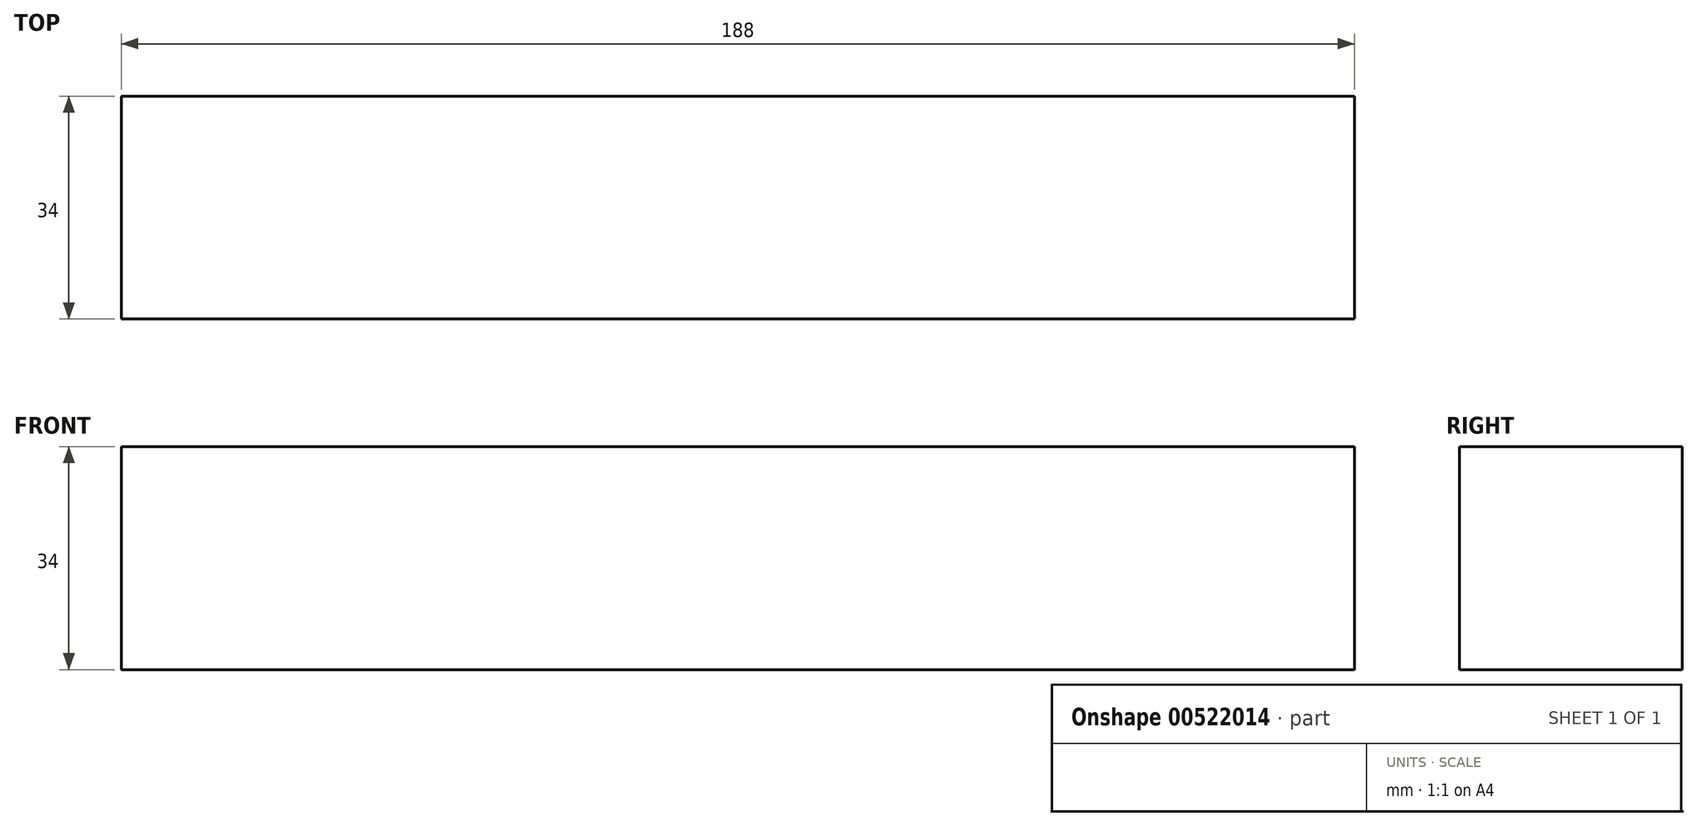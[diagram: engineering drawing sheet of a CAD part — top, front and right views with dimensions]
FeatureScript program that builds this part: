
annotation { "Feature Type Name" : "Feature", "Feature Type Description" : "" }
export const myFeature = defineFeature(function(context is Context, id is Id, definition is map)
    precondition{}
    {
        {
            var Q0;
            Q0=qCreatedBy(makeId("Front.planeOp"),FACE);
            var sketch = newSketch(context, id + "F0", { "sketchPlane" : qUnion([Q0])});
            skLineSegment(sketch, "E0.bottom", {"start": v(0, 0) * mm, "end": v(-188, 0) * mm});
            skLineSegment(sketch, "E0.top", {"start": v(0, 34) * mm, "end": v(-188, 34) * mm});
            skLineSegment(sketch, "E0.left", {"start": v(0, 0) * mm, "end": v(0, 34) * mm});
            skLineSegment(sketch, "E0.right", {"start": v(-188, 0) * mm, "end": v(-188, 34) * mm});
            skSolve(sketch);
        }
        {
            var Q0;
            Q0=makeQuery(id+"F0.imprint","IMPRINT",FACE,{"disambiguationData":[TD([[makeQuery(id+"F0.imprint","IMPRINT",EDGE,{"derivedFrom":sQuery(id+"F0.wireOp",EDGE,"E0.bottom")}),-1.0]])]});
            extrude(context, id + "F1", {"entities" : qUnion([Q0]), "flatOperationType" : FlatOperationType.REMOVE, "depth" : 34 * mm, "offsetDistance" : 25 * mm, "domain" : OperationDomain.MODEL});
        }
    });
